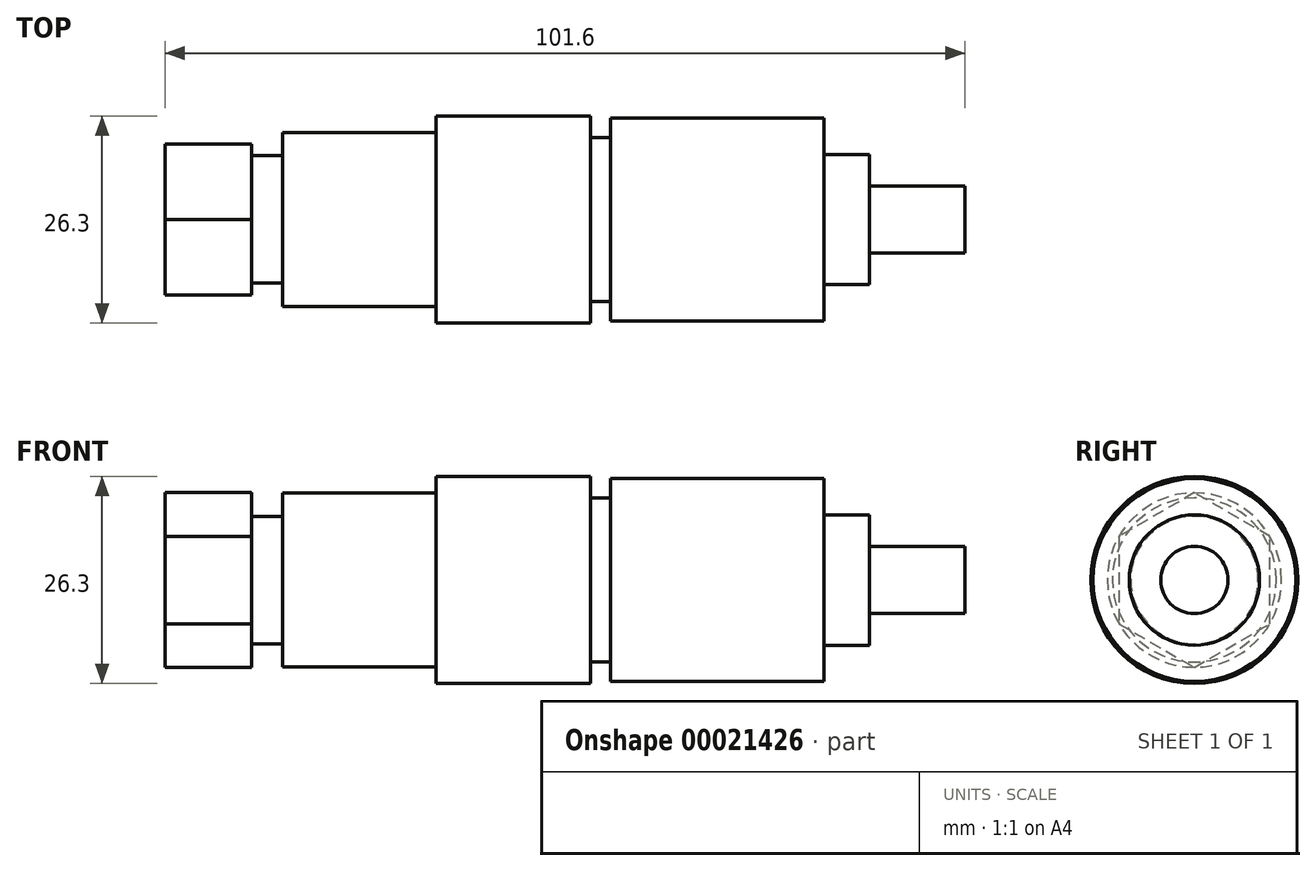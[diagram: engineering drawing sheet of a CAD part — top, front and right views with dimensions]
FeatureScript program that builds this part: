
annotation { "Feature Type Name" : "Feature", "Feature Type Description" : "" }
export const myFeature = defineFeature(function(context is Context, id is Id, definition is map)
    precondition{}
    {
        {
            var Q0;
            Q0=qCreatedBy(makeId("Front.planeOp"),FACE);
            var sketch = newSketch(context, id + "F0", { "sketchPlane" : qUnion([Q0])});
            skLineSegment(sketch, "E0", {"start": v(0, 0) * mm, "end": v(101.6, 0) * mm});
            skLineSegment(sketch, "E1", {"start": v(101.6, 0) * mm, "end": v(101.6, 4.27) * mm});
            skLineSegment(sketch, "E2", {"start": v(101.6, 4.27) * mm, "end": v(89.46, 4.27) * mm});
            skLineSegment(sketch, "E3", {"start": v(89.46, 4.27) * mm, "end": v(89.46, 8.28) * mm});
            skLineSegment(sketch, "E4", {"start": v(89.46, 8.28) * mm, "end": v(83.69, 8.28) * mm});
            skLineSegment(sketch, "E5", {"start": v(83.69, 8.28) * mm, "end": v(83.69, 12.87) * mm});
            skLineSegment(sketch, "E6", {"start": v(83.69, 12.87) * mm, "end": v(56.55, 12.87) * mm});
            skLineSegment(sketch, "E7", {"start": v(56.55, 12.87) * mm, "end": v(56.55, 10.41) * mm});
            skLineSegment(sketch, "E8", {"start": v(56.55, 10.41) * mm, "end": v(54.07, 10.41) * mm});
            skLineSegment(sketch, "E9", {"start": v(54.07, 10.41) * mm, "end": v(54.07, 13.15) * mm});
            skLineSegment(sketch, "E10", {"start": v(54.07, 13.15) * mm, "end": v(34.4, 13.15) * mm});
            skLineSegment(sketch, "E11", {"start": v(34.4, 13.15) * mm, "end": v(34.4, 11.07) * mm});
            skLineSegment(sketch, "E12", {"start": v(34.4, 11.07) * mm, "end": v(14.92, 11.07) * mm});
            skLineSegment(sketch, "E13", {"start": v(14.92, 11.07) * mm, "end": v(14.92, 8.1) * mm});
            skLineSegment(sketch, "E14", {"start": v(14.92, 8.1) * mm, "end": v(10.97, 8.1) * mm});
            skLineSegment(sketch, "E15", {"start": v(10.97, 8.1) * mm, "end": v(10.97, 11.1) * mm});
            skLineSegment(sketch, "E16", {"start": v(10.97, 11.1) * mm, "end": v(0, 11.1) * mm});
            skLineSegment(sketch, "E17", {"start": v(0, 11.1) * mm, "end": v(0, 0) * mm});
            skSolve(sketch);
        }
        {
            var Q0;
            Q0=makeQuery(id+"F0.imprint","IMPRINT",FACE,{"disambiguationData":[TD([[makeQuery(id+"F0.imprint","IMPRINT",EDGE,{"derivedFrom":sQuery(id+"F0.wireOp",EDGE,"E0")}),1.0]])]});
            var Q1;
            Q1=sQuery(id+"F0.wireOp",EDGE,"E0");
            revolve(context, id + "F1", {"entities" : qUnion([Q0]), "axis" : qUnion([Q1]), "revolveType" : RevolveType.FULL});
        }
        {
            var Q0;
            Q0=makeQuery(id+"F1.opRevolve","SWEPT_FACE",FACE,{"disambiguationData":[OSD([sQuery(id+"F0.wireOp",EDGE,"E17")])]});
            var sketch = newSketch(context, id + "F2", { "sketchPlane" : qUnion([Q0])});
            skCircle(sketch, "E18.cCircle", {"center": v(0, 0) * mm, "radius": 11.1 * mm, "construction": true});
            skLineSegment(sketch, "E18.0", {"start": v(0, 11.1) * mm, "end": v(9.6, 5.55) * mm});
            skLineSegment(sketch, "E18.1", {"start": v(9.6, 5.55) * mm, "end": v(9.6, -5.55) * mm});
            skLineSegment(sketch, "E18.2", {"start": v(9.6, -5.55) * mm, "end": v(0, -11.1) * mm});
            skLineSegment(sketch, "E18.3", {"start": v(0, -11.1) * mm, "end": v(-9.6, -5.55) * mm});
            skLineSegment(sketch, "E18.4", {"start": v(-9.6, -5.55) * mm, "end": v(-9.6, 5.55) * mm});
            skLineSegment(sketch, "E18.5", {"start": v(-9.6, 5.55) * mm, "end": v(0, 11.1) * mm});
            skSolve(sketch);
        }
        {
            var Q0;
            {var subQ1=sQuery(id+"F2.wireOp",EDGE,"E18.0");Q0=makeQuery(id+"F2.imprint","IMPRINT",FACE,{"disambiguationData":[TD([[makeQuery(id+"F2.imprint","IMPRINT",EDGE,{"derivedFrom":subQ1}),1.0]])]});}
            var Q1;
            {var subQ1=sQuery(id+"F2.wireOp",EDGE,"E18.1");Q1=makeQuery(id+"F2.imprint","IMPRINT",FACE,{"disambiguationData":[TD([[makeQuery(id+"F2.imprint","IMPRINT",EDGE,{"derivedFrom":subQ1}),1.0]])]});}
            var Q2;
            {var subQ1=sQuery(id+"F2.wireOp",EDGE,"E18.2");Q2=makeQuery(id+"F2.imprint","IMPRINT",FACE,{"disambiguationData":[TD([[makeQuery(id+"F2.imprint","IMPRINT",EDGE,{"derivedFrom":subQ1}),1.0]])]});}
            var Q3;
            {var subQ1=sQuery(id+"F2.wireOp",EDGE,"E18.3");Q3=makeQuery(id+"F2.imprint","IMPRINT",FACE,{"disambiguationData":[TD([[makeQuery(id+"F2.imprint","IMPRINT",EDGE,{"derivedFrom":subQ1}),1.0]])]});}
            var Q4;
            {var subQ1=sQuery(id+"F2.wireOp",EDGE,"E18.4");Q4=makeQuery(id+"F2.imprint","IMPRINT",FACE,{"disambiguationData":[TD([[makeQuery(id+"F2.imprint","IMPRINT",EDGE,{"derivedFrom":subQ1}),1.0]])]});}
            var Q5;
            {var subQ1=sQuery(id+"F2.wireOp",EDGE,"E18.5");Q5=makeQuery(id+"F2.imprint","IMPRINT",FACE,{"disambiguationData":[TD([[makeQuery(id+"F2.imprint","IMPRINT",EDGE,{"derivedFrom":subQ1}),1.0]])]});}
            var Q6;
            Q6=makeQuery(id+"F1.opRevolve","SWEPT_FACE",FACE,{"disambiguationData":[OSD([sQuery(id+"F0.wireOp",EDGE,"E15")])]});
            extrude(context, id + "F3", {"entities" : qUnion([Q0, Q1, Q2, Q3, Q4, Q5]), "operationType" : NewBodyOperationType.REMOVE, "endBound" : BoundingType.UP_TO_SURFACE, "oppositeDirection" : true, "endBoundEntityFace" : qUnion([Q6]), "depth" : 15.24 * mm});
        }
    });
